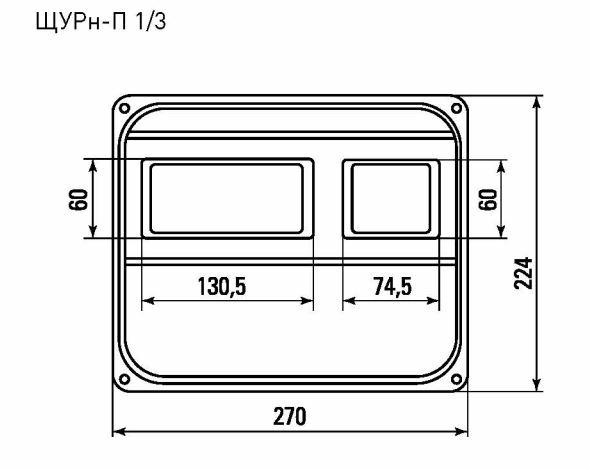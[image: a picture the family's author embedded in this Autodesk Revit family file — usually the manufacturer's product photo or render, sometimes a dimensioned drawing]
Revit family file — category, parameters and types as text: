
# Revit family: EKF_EE_Короб_КЭТ_Транзитный(1890х300х150)_Basic
name_source: partatom
category: Электрооборудование
units: mm (PartAtom-declared; Revit-internal decimal feet)

## family parameters
Всегда вертикально = Да
На основе рабочей плоскости = Нет
Общий = Нет
При загрузке вырезать с полостями = Нет
Размер круглого соединителя = Использовать диаметр
Тип детали = Силовой щит
Точка расчета площади = Да

## types (1)
- Короб КЭТ транзитный (1890х300х150) EKF Basic
    ADSK_Единица измерения = компл.
    ADSK_Завод-изготовитель = EKF
    ADSK_Классификация нагрузок = Прочее
    ADSK_Код изделия = uerm-ket-t-1890
    ADSK_Количество = 1
    ADSK_Количество фаз = 3
    ADSK_Коэффициент мощности = 1
    ADSK_Марка = Короб КЭТ транзитный
    ADSK_Масса = 0
    ADSK_Материал = RAL 7035_Сталь
    ADSK_Наименование = Короб КЭТ транзитный (1890х300х150) EKF BasicКороб КЭТ транзитный (1890х300х150) EKF Basic
    ADSK_Напряжение = 400 В
    ADSK_Номинальная мощность = 0 Вт
    ADSK_Обозначение = Короб КЭТ транзитный
    ADSK_Полная мощность = 0 В·А
    ADSK_Размер_Высота = 1890 мм
    ADSK_Размер_Глубина = 150 мм
    ADSK_Размер_Ширина = 300 мм
    ADSK_Ток = 125 А
    Изготовитель = EKF
    Количество DIN-реек = 0
    Количество модулей на DIN-рейке = 0
    Максимальное количество модулей = 0
    Описание = Короб КЭТ транзитный (1890х300х150) EKF BasicКороб КЭТ транзитный (1890х300х150) EKF Basic
    Серия номенклатуры = Basic
    Степень защиты IP = IP31
    ТВ = EKF
    Тип = 204 мм
    Тип установки = Навесной
